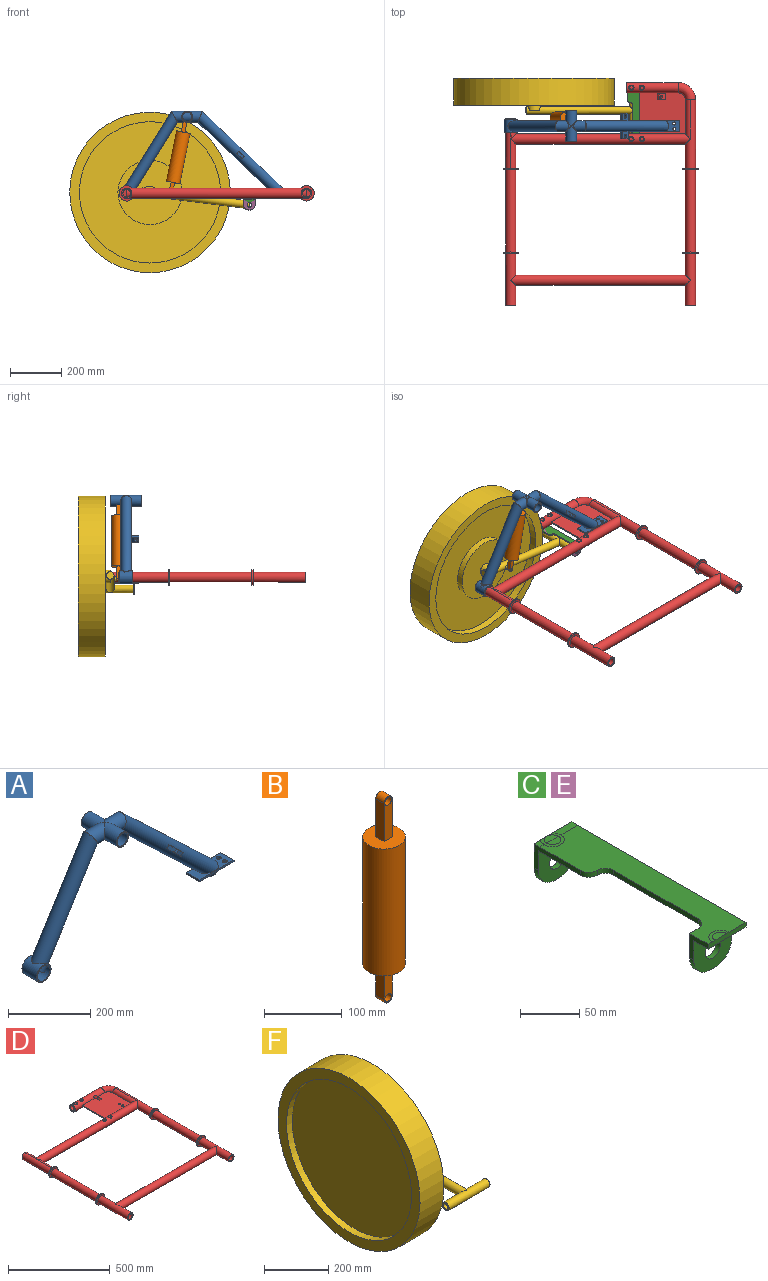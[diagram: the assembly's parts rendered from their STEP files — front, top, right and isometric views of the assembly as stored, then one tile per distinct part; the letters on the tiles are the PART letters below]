
ASSEMBLY  parts=6 mates=3
PART A: 62 faces, bbox 682.4x120x344.5 mm
  f0: cylinder r=18mm len=48.8mm, axis (0,-1,0), area 4910.4mm2, adj f2,f32
  f1: cylinder r=21.2mm len=60mm, axis (0,-1,0), area 6194.5mm2, adj f2,f13,f26
  f2: plane 42.4x42.4mm, normal (0,1,0), area 394.1mm2, adj f0,f1
  f3: cylinder r=21.2mm len=42.4mm, axis (0.73,0,-0.69), area 1202.5mm2, adj f5,f6
  f4: cylinder r=19mm len=38mm, axis (0.73,0,-0.69), area 990.8mm2, adj f5,f6
  f5: plane 42.4x17.88mm, normal (0.73,0,-0.69), area 154.2mm2, adj f3,f4,f6
  f6: plane 120x45mm, normal (0,0,-1), area 4949.8mm2, adj f3,f4,f5,f7,f8,f9,f10,f53
  f7: plane 120x5mm, normal (0,1,0), area 600mm2, adj f6,f8,f10,f11
  f8: plane 45x5mm, normal (1,0,0), area 225mm2, adj f6,f7,f9,f11
  f9: plane 120x5mm, normal (0,-1,0), area 600mm2, adj f6,f8,f10,f11
  f10: plane 45x5mm, normal (-1,0,0), area 225mm2, adj f6,f7,f9,f11
  f11: plane 120x45mm, normal (0,0,1), area 4902.5mm2, adj f7,f8,f9,f10,f12,f14,f15,f53
  f12: cylinder r=21.2mm len=349.84mm, axis (0.73,0,-0.69), area 55328.1mm2, adj f11,f13,f14,f38,f39,f40,f41,f42
  f13: cylinder r=21.2mm len=58.46mm, axis (1,0,0), area 4847.4mm2, adj f1,f12,f20
  f14: plane 37.02x7.88mm, normal (0.73,0,-0.69), area 91.1mm2, adj f11,f12,f15
  f15: cylinder r=19mm len=346.17mm, axis (0.73,0,-0.69), area 49651.3mm2, adj f11,f14,f16,f33,f34,f35,f36
  f16: cylinder r=19mm len=48.17mm, axis (1,0,0), area 4114.2mm2, adj f15,f17
  f17: cylinder r=21.2mm len=38mm, axis (0,-1,0), area 1311.6mm2, adj f16
  f18: cylinder r=18mm len=48.8mm, axis (0,-1,0), area 4909mm2, adj f19,f31
  f19: plane 42.4x42.4mm, normal (0,-1,0), area 394.1mm2, adj f18,f20
  f20: cylinder r=21.2mm len=60mm, axis (0,-1,0), area 6194.5mm2, adj f13,f19,f26
  f21: cylinder r=21.5mm len=38mm, axis (0,1,0), area 1304.9mm2, adj f24
  f22: cylinder r=21.2mm len=47.36mm, axis (0.53,0,0.85), area 1892mm2, adj f23,f30
  f23: plane 42.4x36.01mm, normal (-0.53,0,-0.85), area 277.8mm2, adj f22,f24
  f24: cylinder r=19mm len=43.62mm, axis (0.53,0,0.85), area 1946.5mm2, adj f21,f23
  f25: cylinder r=21.2mm len=319.4mm, axis (0.53,0,0.85), area 44162.7mm2, adj f26,f29
  f26: cylinder r=21.2mm len=61.78mm, axis (1,0,0), area 4849.1mm2, adj f1,f20,f25
  f27: plane 50x50mm, normal (0,1,0), area 511.3mm2, adj f29,f30
  f28: plane 50x50mm, normal (0,-1,0), area 511.3mm2, adj f29,f30
  f29: cylinder r=25mm len=50mm, axis (0,1,0), area 6256.8mm2, adj f25,f27,f28
  f30: cylinder r=21.5mm len=50mm, axis (0,1,0), area 5000.3mm2, adj f22,f27,f28
  f31: cylinder r=21.2mm len=36mm, axis (1,0,0), area 1152.3mm2, adj f18
  f32: cylinder r=21.2mm len=36mm, axis (1,0,0), area 1151.2mm2, adj f0
  f33: plane 38x7.26mm, normal (-0.73,0,0.69), area 375.6mm2, adj f15,f34,f36
  f34: plane 36.66x21.77mm, normal (0.69,0,0.73), area 1099.8mm2, adj f15,f33,f35
  f35: plane 38x7.26mm, normal (0.73,0,-0.69), area 375.6mm2, adj f15,f34,f36
  f36: plane 36.66x21.77mm, normal (-0.69,0,-0.73), area 1099.8mm2, adj f15,f33,f35
  f37: plane 21.39x21.02mm, normal (0,1,0), area 200mm2, adj f39,f41,f47,f48
  f38: plane 24.4x7.26mm, normal (-0.73,0,0.69), area 240mm2, adj f12,f39,f41,f48
  f39: plane 29.4x21.77mm, normal (0.69,0,0.73), area 717.3mm2, adj f12,f37,f38,f40,f47,f48,f52
  f40: plane 24.4x7.26mm, normal (0.73,0,-0.69), area 240mm2, adj f12,f39,f41,f47
  f41: plane 29.4x21.77mm, normal (-0.69,0,-0.73), area 717.3mm2, adj f12,f37,f38,f40,f47,f48,f52
  f42: plane 29.4x21.77mm, normal (-0.69,0,-0.73), area 717.3mm2, adj f12,f43,f45,f46,f49,f50,f51
  f43: plane 24.4x7.26mm, normal (0.73,0,-0.69), area 240mm2, adj f12,f42,f44,f49
  f44: plane 29.4x21.77mm, normal (0.69,0,0.73), area 717.3mm2, adj f12,f43,f45,f46,f49,f50,f51
  f45: plane 24.4x7.26mm, normal (-0.73,0,0.69), area 240mm2, adj f12,f42,f44,f50
  f46: plane 21.39x21.02mm, normal (0,-1,0), area 200mm2, adj f42,f44,f49,f50
  f47: cylinder r=5mm len=10.7mm, axis (0.69,0,0.73), area 78.5mm2, adj f37,f39,f40,f41
  f48: cylinder r=5mm len=10.7mm, axis (-0.69,0,-0.73), area 78.5mm2, adj f37,f38,f39,f41
  f49: cylinder r=5mm len=10.7mm, axis (-0.69,0,-0.73), area 78.5mm2, adj f42,f43,f44,f46
  f50: cylinder r=5mm len=10.7mm, axis (0.69,0,0.73), area 78.5mm2, adj f42,f44,f45,f46
  f51: cylinder r=7mm len=17.04mm, axis (0.69,0,0.73), area 439.8mm2, adj f42,f44
  f52: cylinder r=7mm len=17.04mm, axis (0.69,0,0.73), area 439.8mm2, adj f39,f41
  f53: cylinder r=6mm len=12mm, axis (0,0,1), area 188.5mm2, adj f6,f11
  f54: cylinder r=6mm len=12mm, axis (0,0,1), area 188.5mm2, adj f6,f11
  f55: cylinder r=18mm len=38mm, axis (0,-1,0), area 3028mm2, adj f56,f57
  f56: cylinder r=19mm len=36mm, axis (1,0,0), area 1218.3mm2, adj f55
  f57: cylinder r=19mm len=36mm, axis (1,0,0), area 1218.9mm2, adj f55
  f58: cylinder r=25mm len=38mm, axis (0,1,0), area 1242.2mm2, adj f59
  f59: cylinder r=19mm len=313.49mm, axis (0.53,0,0.85), area 39430.5mm2, adj f58,f60
  f60: cylinder r=19mm len=51.16mm, axis (1,0,0), area 4066.1mm2, adj f59,f61
  f61: cylinder r=21.2mm len=38mm, axis (0,-1,0), area 1313.4mm2, adj f60
PART B: 15 faces, bbox 55x55x325 mm
  f0: cylinder r=7.5mm len=15mm, axis (0,1,0), area 353.4mm2, adj f1,f2,f4,f5
  f1: plane 60x15mm, normal (-1,0,0), area 900mm2, adj f0,f4,f5,f7
  f2: plane 60x15mm, normal (1,0,0), area 900mm2, adj f0,f4,f5,f7
  f3: cylinder r=6mm len=15mm, axis (0,1,0), area 565.5mm2, adj f4,f5
  f4: plane 67.5x15mm, normal (0,-1,0), area 875.3mm2, adj f0,f1,f2,f3,f7
  f5: plane 67.5x15mm, normal (0,1,0), area 875.3mm2, adj f0,f1,f2,f3,f7
  f6: cylinder r=27.5mm len=200mm, axis (0,0,-1), area 34557.5mm2, adj f7,f8
  f7: plane 55x55mm, normal (0,0,1), area 2150.8mm2, adj f1,f2,f4,f5,f6
  f8: plane 55x55mm, normal (0,0,-1), area 2150.8mm2, adj f6,f11,f12,f13,f14
  f9: cylinder r=7.5mm len=15mm, axis (0,1,0), area 353.4mm2, adj f11,f12,f13,f14
  f10: cylinder r=6mm len=15mm, axis (0,1,0), area 565.5mm2, adj f11,f12
  f11: plane 57.5x15mm, normal (0,-1,0), area 725.3mm2, adj f8,f9,f10,f13,f14
  f12: plane 57.5x15mm, normal (0,1,0), area 725.3mm2, adj f8,f9,f10,f13,f14
  f13: plane 50x15mm, normal (1,0,0), area 750mm2, adj f8,f9,f11,f12
  f14: plane 50x15mm, normal (-1,0,0), area 750mm2, adj f8,f9,f11,f12
PART C: 30 faces, bbox 45x207x45 mm
  f0: plane 22.86x7mm, normal (0,0,1), area 146.2mm2, adj f2,f3,f6,f17
  f1: plane 7.86x7mm, normal (0,0,1), area 41.2mm2, adj f2,f5,f6,f17
  f2: plane 20x17mm, normal (0,0,1), area 130.7mm2, adj f0,f1,f6,f8,f17,f21
  f3: plane 207x25mm, normal (1,0,0), area 1235mm2, adj f0,f4,f6,f10,f12,f13,f15,f17
  f4: plane 45x40mm, normal (0,-1,0), area 1373.8mm2, adj f3,f5,f7,f9,f10,f11,f12
  f5: plane 55x25mm, normal (-1,0,0), area 375mm2, adj f1,f4,f6,f9,f12,f17,f22
  f6: plane 45x45mm, normal (0,1,0), area 1598.8mm2, adj f0,f1,f2,f3,f5,f7,f9,f10
  f7: plane 5x5mm, normal (0,0,-1), area 25mm2, adj f4,f6,f9,f10
  f8: plane 14x7mm, normal (0,0,1), area 77mm2, adj f2,f21
  f9: cylinder r=20mm len=20mm, axis (0,-1,0), area 157.1mm2, adj f4,f5,f6,f7
  f10: cylinder r=20mm len=20mm, axis (0,1,0), area 157.1mm2, adj f3,f4,f6,f7
  f11: cylinder r=9mm len=18mm, axis (0,1,0), area 282.7mm2, adj f4,f6
  f12: plane 180x45mm, normal (0,0,-1), area 5721.5mm2, adj f3,f4,f5,f15,f22,f23,f24,f25
  f13: plane 45x40mm, normal (0,-1,0), area 1373.8mm2, adj f3,f14,f16,f18,f19,f20,f26
  f14: plane 25x22mm, normal (-1,0,0), area 210mm2, adj f13,f15,f17,f18,f26,f29
  f15: plane 45x45mm, normal (0,1,0), area 1423.8mm2, adj f3,f12,f14,f16,f17,f18,f19,f20
  f16: plane 5x5mm, normal (0,0,-1), area 25mm2, adj f13,f15,f18,f19
  f17: plane 200x45mm, normal (0,0,1), area 6307.3mm2, adj f0,f1,f2,f3,f5,f14,f15,f22
  f18: cylinder r=20mm len=20mm, axis (0,-1,0), area 157.1mm2, adj f13,f14,f15,f16
  f19: cylinder r=20mm len=20mm, axis (0,1,0), area 157.1mm2, adj f3,f13,f15,f16
  f20: cylinder r=9mm len=18mm, axis (0,1,0), area 282.7mm2, adj f13,f15
  f21: plane 14x7mm, normal (0,0,1), area 77mm2, adj f2,f8
  f22: cylinder r=10mm len=10mm, axis (0,0,1), area 78.5mm2, adj f5,f12,f17,f23
  f23: cylinder r=10mm len=10mm, axis (0,0,1), area 78.5mm2, adj f12,f17,f22,f24
  f24: plane 100x5mm, normal (-1,0,0), area 500mm2, adj f12,f17,f23,f25
  f25: cylinder r=10mm len=10mm, axis (0,0,1), area 78.5mm2, adj f12,f15,f17,f24
  f26: plane 45x17mm, normal (0,0,-1), area 765mm2, adj f3,f13,f14,f29
  f27: plane 20x10mm, normal (0,0,1), area 80.1mm2, adj f17,f28,f29
  f28: plane 14x7mm, normal (0,0,1), area 77mm2, adj f27,f29
  f29: plane 45x5mm, normal (0,-1,0), area 225mm2, adj f3,f14,f17,f26,f27,f28
PART D: 178 faces, bbox 760x875.6x60 mm
  f0: plane 20x10mm, normal (0,0,-1), area 80.1mm2, adj f64,f66,f67
  f1: plane 14.28x3mm, normal (0,0,-1), area 29.5mm2, adj f16,f17
  f2: cylinder r=20mm len=14mm, axis (-1,0,0), area 78.2mm2, adj f9,f19
  f3: cylinder r=20mm len=14mm, axis (-1,0,0), area 78.2mm2, adj f62,f63
  f4: cylinder r=15mm len=30mm, axis (1,0,0), area 450mm2, adj f6,f132
  f5: cylinder r=20mm len=30mm, axis (1,0,0), area 385.9mm2, adj f6,f120
  f6: plane 30x20mm, normal (-1,0,0), area 184.2mm2, adj f4,f5,f120
  f7: cylinder r=10mm len=30mm, axis (0,0,-1), area 1653.8mm2, adj f118
  f8: cylinder r=20mm len=14mm, axis (-1,0,0), area 156.4mm2, adj f10,f11
  f9: cylinder r=20mm len=14mm, axis (-1,0,0), area 78.2mm2, adj f2,f18
  f10: cylinder r=7mm len=14mm, axis (0,0,-1), area 13.8mm2, adj f8,f14
  f11: cylinder r=7mm len=14mm, axis (0,0,-1), area 13.8mm2, adj f8,f14
  f12: cylinder r=10mm len=20mm, axis (0,0,-1), area 41.3mm2, adj f14,f117
  f13: cylinder r=10mm len=20mm, axis (0,0,-1), area 41.3mm2, adj f14,f117
  f14: plane 20x20mm, normal (0,0,1), area 160.2mm2, adj f10,f11,f12,f13
  f15: cylinder r=10mm len=20mm, axis (0,0,-1), area 41.3mm2, adj f16,f117
  f16: plane 20x17mm, normal (0,0,-1), area 130.7mm2, adj f1,f15,f17,f18,f19
  f17: cylinder r=10mm len=20mm, axis (0,0,-1), area 41.3mm2, adj f1,f16,f117
  f18: cylinder r=7mm len=14mm, axis (0,0,-1), area 13.8mm2, adj f9,f16
  f19: cylinder r=7mm len=14mm, axis (0,0,-1), area 13.8mm2, adj f2,f16
  f20: cylinder r=20mm len=14mm, axis (-1,0,0), area 156.4mm2, adj f24,f25
  f21: cylinder r=20mm len=14mm, axis (-1,0,0), area 156.4mm2, adj f30,f31
  f22: cylinder r=10mm len=20mm, axis (0,0,-1), area 41.3mm2, adj f26,f116
  f23: cylinder r=10mm len=20mm, axis (0,0,-1), area 41.3mm2, adj f26,f116
  f24: cylinder r=7mm len=14mm, axis (0,0,-1), area 13.8mm2, adj f20,f26
  f25: cylinder r=7mm len=14mm, axis (0,0,-1), area 13.8mm2, adj f20,f26
  f26: plane 20x20mm, normal (0,0,1), area 160.2mm2, adj f22,f23,f24,f25
  f27: cylinder r=10mm len=20mm, axis (0,0,-1), area 41.3mm2, adj f28,f116
  f28: plane 20x20mm, normal (0,0,-1), area 160.2mm2, adj f27,f29,f30,f31
  f29: cylinder r=10mm len=20mm, axis (0,0,-1), area 41.3mm2, adj f28,f116
  f30: cylinder r=7mm len=14mm, axis (0,0,-1), area 13.8mm2, adj f21,f28
  f31: cylinder r=7mm len=14mm, axis (0,0,-1), area 13.8mm2, adj f21,f28
  f32: cylinder r=20mm len=14mm, axis (-1,0,0), area 156.4mm2, adj f37,f38
  f33: cylinder r=20mm len=14mm, axis (-1,0,0), area 156.4mm2, adj f42,f43
  f34: cylinder r=10mm len=20mm, axis (0,0,-1), area 41.3mm2, adj f36,f117
  f35: cylinder r=10mm len=20mm, axis (0,0,-1), area 41.3mm2, adj f36,f117
  f36: plane 20x20mm, normal (0,0,1), area 160.2mm2, adj f34,f35,f37,f38
  f37: cylinder r=7mm len=14mm, axis (0,0,-1), area 13.8mm2, adj f32,f36
  f38: cylinder r=7mm len=14mm, axis (0,0,-1), area 13.8mm2, adj f32,f36
  f39: cylinder r=10mm len=20mm, axis (0,0,-1), area 41.3mm2, adj f40,f117
  f40: plane 20x20mm, normal (0,0,-1), area 160.2mm2, adj f39,f41,f42,f43
  f41: cylinder r=10mm len=20mm, axis (0,0,-1), area 41.3mm2, adj f40,f117
  f42: cylinder r=7mm len=14mm, axis (0,0,-1), area 13.8mm2, adj f33,f40
  f43: cylinder r=7mm len=14mm, axis (0,0,-1), area 13.8mm2, adj f33,f40
  f44: plane 160.31x5mm, normal (-1,0,0), area 800.5mm2, adj f45,f46,f116,f117
  f45: plane 180.16x160.31mm, normal (0,0,1), area 28184.4mm2, adj f44,f107,f108,f116,f117,f133,f134,f140
  f46: plane 180.16x160.31mm, normal (0,0,-1), area 28434.8mm2, adj f44,f107,f109,f116,f117,f133,f134,f135
  f47: cylinder r=10mm len=30mm, axis (0,0,-1), area 1496.7mm2, adj f48,f49,f50,f51,f118
  f48: plane 15x5mm, normal (-1,0,0), area 74.7mm2, adj f47,f49,f50,f118
  f49: plane 200x180.16mm, normal (0,0,1), area 4992.2mm2, adj f47,f48,f51,f52,f105,f106,f111,f112
  f50: plane 200x180.16mm, normal (0,0,-1), area 4992.2mm2, adj f47,f48,f51,f52,f105,f111,f113,f115
  f51: plane 132.5x5mm, normal (0,1,0), area 662.5mm2, adj f47,f49,f50,f52
  f52: cylinder r=47.5mm len=47.5mm, axis (0,0,-1), area 373.1mm2, adj f49,f50,f51,f105
  f53: plane 15x5mm, normal (0,-1,0), area 74.7mm2, adj f54,f55,f100,f105
  f54: plane 14.79x14.79mm, normal (0,0,1), area 218.7mm2, adj f53,f100,f104,f105
  f55: plane 14.79x14.79mm, normal (0,0,-1), area 218.7mm2, adj f53,f100,f105,f114
  f56: cylinder r=20mm len=14mm, axis (-1,0,0), area 156.4mm2, adj f57,f58
  f57: cylinder r=7mm len=14mm, axis (0,0,-1), area 13.8mm2, adj f56,f61
  f58: cylinder r=7mm len=14mm, axis (0,0,-1), area 13.8mm2, adj f56,f61
  f59: cylinder r=10mm len=20mm, axis (0,0,-1), area 41.3mm2, adj f61,f116
  f60: cylinder r=10mm len=20mm, axis (0,0,-1), area 41.3mm2, adj f61,f116
  f61: plane 20x20mm, normal (0,0,1), area 160.2mm2, adj f57,f58,f59,f60
  f62: cylinder r=20mm len=14mm, axis (-1,0,0), area 78.2mm2, adj f3,f66
  f63: cylinder r=7mm len=14mm, axis (0,0,-1), area 13.8mm2, adj f3,f64
  f64: plane 20x10mm, normal (0,0,-1), area 80.1mm2, adj f0,f63,f65
  f65: cylinder r=10mm len=20mm, axis (0,0,-1), area 41.3mm2, adj f64,f116
  f66: cylinder r=7mm len=14mm, axis (0,0,-1), area 13.8mm2, adj f0,f62
  f67: cylinder r=10mm len=20mm, axis (0,0,-1), area 41.3mm2, adj f0,f116
  f68: cylinder r=20mm len=320mm, axis (0,1,0), area 40212.4mm2, adj f69,f78
  f69: plane 60x60mm, normal (0,1,0), area 1570.8mm2, adj f68,f70
  f70: cylinder r=30mm len=60mm, axis (0,1,0), area 942.5mm2, adj f69,f71
  f71: plane 60x60mm, normal (0,-1,0), area 1570.8mm2, adj f70,f72
  f72: cylinder r=20mm len=205mm, axis (0,1,0), area 24161.1mm2, adj f71,f73,f121
  f73: plane 40x40mm, normal (0,-1,0), area 549.8mm2, adj f72,f119
  f74: plane 30x30mm, normal (0,-1,0), area 706.9mm2, adj f119
  f75: plane 30x30mm, normal (0,1,0), area 706.9mm2, adj f113
  f76: cylinder r=30mm len=60mm, axis (0,-1,0), area 942.5mm2, adj f77,f78
  f77: plane 60x60mm, normal (0,1,0), area 1570.8mm2, adj f76,f109
  f78: plane 60x60mm, normal (0,-1,0), area 1570.8mm2, adj f68,f76
  f79: cylinder r=15mm len=30.1mm, axis (0,1,0), area 900mm2, adj f82,f85
  f80: cylinder r=20mm len=30mm, axis (-1,0,0), area 386mm2, adj f81,f98
  f81: plane 30x20mm, normal (-1,0,0), area 184.2mm2, adj f80,f82,f98
  f82: cylinder r=15mm len=30mm, axis (-1,0,0), area 450mm2, adj f79,f81
  f83: cylinder r=20mm len=30mm, axis (-1,0,0), area 386mm2, adj f84,f98
  f84: plane 30x20mm, normal (-1,0,0), area 184.2mm2, adj f83,f85,f98
  f85: cylinder r=15mm len=30mm, axis (-1,0,0), area 450mm2, adj f79,f84
  f86: plane 30x30mm, normal (0,-1,0), area 706.9mm2, adj f120
  f87: plane 40x40mm, normal (0,-1,0), area 549.8mm2, adj f88,f120
  f88: cylinder r=20mm len=205mm, axis (0,1,0), area 24161.1mm2, adj f87,f96,f121
  f89: plane 40x40mm, normal (0,1,0), area 549.8mm2, adj f98,f99
  f90: plane 60x60mm, normal (0,-1,0), area 1570.8mm2, adj f92,f94
  f91: plane 60x60mm, normal (0,1,0), area 1570.8mm2, adj f92,f99
  f92: cylinder r=30mm len=60mm, axis (0,-1,0), area 942.5mm2, adj f90,f91
  f93: plane 30x30mm, normal (0,1,0), area 706.9mm2, adj f98
  f94: cylinder r=20mm len=320mm, axis (0,1,0), area 40212.4mm2, adj f90,f95
  f95: plane 60x60mm, normal (0,1,0), area 1570.8mm2, adj f94,f97
  f96: plane 60x60mm, normal (0,-1,0), area 1570.8mm2, adj f88,f97
  f97: cylinder r=30mm len=60mm, axis (0,1,0), area 942.5mm2, adj f95,f96
  f98: cylinder r=15mm len=195mm, axis (0,1,0), area 16796.1mm2, adj f80,f81,f83,f84,f89,f93
  f99: cylinder r=20mm len=195mm, axis (0,1,0), area 22904.4mm2, adj f89,f91,f116
  f100: cylinder r=15mm len=30mm, axis (0,1,0), area 825mm2, adj f53,f54,f55,f103,f104,f114
  f101: cylinder r=20mm len=30mm, axis (-1,0,0), area 386mm2, adj f102,f113
  f102: plane 30x20mm, normal (1,0,0), area 184.2mm2, adj f101,f103,f113
  f103: cylinder r=15mm len=30mm, axis (-1,0,0), area 450mm2, adj f100,f102
  f104: cylinder r=15mm len=14.79mm, axis (-1,0,0), area 187.5mm2, adj f54,f100,f105
  f105: plane 152.5x30mm, normal (1,0,0), area 921.6mm2, adj f49,f50,f52,f53,f54,f55,f104,f106
  f106: cylinder r=20mm len=14.79mm, axis (-1,0,0), area 155.5mm2, adj f49,f105,f112
  f107: torus R=47.5mm, axis (0,0,1), area 9159.2mm2, adj f45,f46,f108,f109,f117
  f108: cylinder r=20mm len=152.5mm, axis (0,1,0), area 4058.7mm2, adj f45,f107,f109,f116
  f109: cylinder r=20mm len=267.5mm, axis (0,1,0), area 27291.9mm2, adj f46,f77,f107,f108,f116
  f110: plane 40x40mm, normal (-1,0,0), area 549.8mm2, adj f117,f118
  f111: torus R=47.5mm, axis (0,0,1), area 6775.1mm2, adj f49,f50,f112,f113,f118
  f112: cylinder r=15mm len=139.27mm, axis (0,1,0), area 2864.7mm2, adj f49,f106,f111,f113
  f113: cylinder r=15mm len=267.5mm, axis (0,1,0), area 20098.5mm2, adj f50,f75,f101,f102,f105,f111,f112,f115
  f114: cylinder r=15mm len=14.79mm, axis (-1,0,0), area 187.5mm2, adj f55,f100,f105
  f115: cylinder r=20mm len=14.79mm, axis (-1,0,0), area 155.5mm2, adj f50,f105,f113
  f116: cylinder r=20mm len=700mm, axis (-1,0,0), area 82561.9mm2, adj f22,f23,f27,f29,f44,f45,f46,f59
  f117: cylinder r=20mm len=202.5mm, axis (-1,0,0), area 23382.6mm2, adj f12,f13,f15,f17,f34,f35,f39,f41
  f118: cylinder r=15mm len=202.5mm, axis (-1,0,0), area 16979.3mm2, adj f7,f47,f48,f49,f50,f110,f111
  f119: cylinder r=15mm len=205mm, axis (0,1,0), area 17738.6mm2, adj f73,f74,f122,f123,f125,f126
  f120: cylinder r=15mm len=205mm, axis (0,1,0), area 17738.6mm2, adj f5,f6,f86,f87,f128,f129
  f121: cylinder r=20mm len=700mm, axis (1,0,0), area 84764.6mm2, adj f72,f88
  f122: cylinder r=20mm len=30mm, axis (1,0,0), area 386mm2, adj f119,f123
  f123: plane 30x20mm, normal (1,0,0), area 184.2mm2, adj f119,f122,f124
  f124: cylinder r=15mm len=30mm, axis (1,0,0), area 450mm2, adj f123,f131
  f125: cylinder r=20mm len=30mm, axis (1,0,0), area 386mm2, adj f119,f126
  f126: plane 30x20mm, normal (1,0,0), area 184.2mm2, adj f119,f125,f127
  f127: cylinder r=15mm len=30mm, axis (1,0,0), area 450mm2, adj f126,f131
  f128: cylinder r=20mm len=30mm, axis (1,0,0), area 385.9mm2, adj f120,f129
  f129: plane 30x20mm, normal (-1,0,0), area 184.2mm2, adj f120,f128,f130
  f130: cylinder r=15mm len=30mm, axis (1,0,0), area 450mm2, adj f129,f132
  f131: cylinder r=15mm len=30.1mm, axis (0,1,0), area 900mm2, adj f124,f127
  f132: cylinder r=15mm len=30.1mm, axis (0,1,0), area 900mm2, adj f4,f130
  f133: cylinder r=6mm len=12mm, axis (0,0,1), area 188.5mm2, adj f45,f46
  f134: cylinder r=6mm len=12mm, axis (0,0,1), area 188.5mm2, adj f45,f46
  f135: plane 25x1.19mm, normal (-0.69,0,-0.73), area 41mm2, adj f46,f136,f137,f138
  f136: plane 2.26x1.13mm, normal (0,1,0), area 1.3mm2, adj f46,f135,f137
  f137: plane 25x1.13mm, normal (0.73,0,-0.69), area 38.9mm2, adj f46,f135,f136,f138
  f138: plane 2.26x1.13mm, normal (0,-1,0), area 1.3mm2, adj f46,f135,f137
  f139: plane 15x7.26mm, normal (-0.73,0,0.69), area 150mm2, adj f144,f145,f146,f147
  f140: plane 28.65x21.77mm, normal (0,-1,0), area 262.4mm2, adj f45,f141,f144,f145,f146
  f141: plane 25x1.13mm, normal (0.73,0,-0.69), area 38.9mm2, adj f45,f140,f143,f145
  f142: cylinder r=6mm len=15.59mm, axis (0.69,0,0.73), area 377mm2, adj f144,f145
  f143: plane 28.65x21.77mm, normal (0,1,0), area 262.4mm2, adj f45,f141,f144,f145,f147
  f144: plane 25x18.93mm, normal (-0.69,0,-0.73), area 528.5mm2, adj f45,f139,f140,f142,f143,f146,f147
  f145: plane 25.4x25mm, normal (0.69,0,0.73), area 751.2mm2, adj f139,f140,f141,f142,f143,f146,f147
  f146: cylinder r=5mm len=10.7mm, axis (-0.69,0,-0.73), area 78.5mm2, adj f139,f140,f144,f145
  f147: cylinder r=5mm len=10.7mm, axis (0.69,0,0.73), area 78.5mm2, adj f139,f143,f144,f145
  f148: cylinder r=20mm len=30mm, axis (0,1,0), area 772mm2, adj f149
  f149: cylinder r=15mm len=673.55mm, axis (1,0,0), area 62809mm2, adj f148,f150
  f150: cylinder r=20mm len=30mm, axis (0,1,0), area 771.9mm2, adj f149
  f151: cylinder r=7mm len=30mm, axis (0,0,-1), area 1244.4mm2, adj f152,f153
  f152: cylinder r=15mm len=14mm, axis (-1,0,0), area 158.5mm2, adj f151
  f153: cylinder r=15mm len=14mm, axis (-1,0,0), area 158.5mm2, adj f151
  f154: cylinder r=7mm len=30mm, axis (0,0,-1), area 1244.4mm2, adj f155,f156
  f155: cylinder r=15mm len=14mm, axis (-1,0,0), area 158.5mm2, adj f154
  f156: cylinder r=15mm len=14mm, axis (-1,0,0), area 158.5mm2, adj f154
  f157: cylinder r=7mm len=30mm, axis (0,0,-1), area 1244.4mm2, adj f158,f159
  f158: cylinder r=15mm len=14mm, axis (-1,0,0), area 158.5mm2, adj f157
  f159: cylinder r=15mm len=14mm, axis (-1,0,0), area 158.5mm2, adj f157
  f160: plane 30x30mm, normal (0,1,0), area 706.9mm2, adj f161
  f161: cylinder r=15mm len=320mm, axis (0,1,0), area 30159.3mm2, adj f160,f162
  f162: plane 30x30mm, normal (0,-1,0), area 706.9mm2, adj f161
  f163: cylinder r=15mm len=673.55mm, axis (-1,0,0), area 60565.1mm2, adj f164,f165,f166,f167,f168,f170,f171
  f164: cylinder r=20mm len=30mm, axis (0,1,0), area 772.1mm2, adj f163
  f165: cylinder r=20mm len=30mm, axis (0,1,0), area 696.9mm2, adj f163,f167,f168,f169
  f166: cylinder r=10mm len=30mm, axis (0,0,-1), area 1653.8mm2, adj f163
  f167: plane 180.16x14.79mm, normal (0,0,1), area 2507.5mm2, adj f163,f165,f169,f170,f171
  f168: plane 180.16x14.79mm, normal (0,0,-1), area 2507.5mm2, adj f163,f165,f169,f170,f171
  f169: plane 160.16x5mm, normal (0,-1,0), area 800.3mm2, adj f165,f167,f168,f171
  f170: plane 15x5mm, normal (-1,0,0), area 74.7mm2, adj f163,f167,f168,f171
  f171: cylinder r=10mm len=30mm, axis (0,0,-1), area 1496.7mm2, adj f163,f167,f168,f169,f170
  f172: plane 30x30mm, normal (0,-1,0), area 706.9mm2, adj f173
  f173: cylinder r=15mm len=320mm, axis (0,1,0), area 30159.3mm2, adj f172,f174
  f174: plane 30x30mm, normal (0,1,0), area 706.9mm2, adj f173
  f175: cylinder r=7mm len=30mm, axis (0,0,-1), area 1244.4mm2, adj f176,f177
  f176: cylinder r=15mm len=14mm, axis (-1,0,0), area 158.5mm2, adj f175
  f177: cylinder r=15mm len=14mm, axis (-1,0,0), area 158.5mm2, adj f175
PART E: same geometry as C
PART F: 23 faces, bbox 215x717.5x625 mm
  f0: cylinder r=15mm len=420mm, axis (0,1,0), area 36441.3mm2, adj f4,f5,f9,f10,f11,f21
  f1: cylinder r=9.5mm len=180mm, axis (1,0,0), area 9946.9mm2, adj f2,f3,f6,f7,f8
  f2: plane 30x30mm, normal (-1,0,0), area 423.3mm2, adj f1,f4
  f3: plane 30x30mm, normal (1,0,0), area 423.3mm2, adj f1,f4
  f4: cylinder r=15mm len=180mm, axis (1,0,0), area 16064.6mm2, adj f0,f2,f3
  f5: plane 30x30mm, normal (0,1,0), area 706.9mm2, adj f0
  f6: cylinder r=15mm len=19mm, axis (0,1,0), area 150.2mm2, adj f1,f8
  f7: cylinder r=15mm len=19mm, axis (0,1,0), area 150.2mm2, adj f1,f8
  f8: plane 30x19mm, normal (0,-1,0), area 529.2mm2, adj f1,f6,f7
  f9: plane 40x10mm, normal (1,0,0), area 279.6mm2, adj f0,f10
  f10: cylinder r=25mm len=50mm, axis (1,0,0), area 3182.5mm2, adj f0,f9,f11,f13
  f11: plane 40x10mm, normal (1,0,0), area 279.6mm2, adj f0,f10
  f12: cylinder r=125mm len=250mm, axis (1,0,0), area 19635mm2, adj f13,f14
  f13: plane 250x250mm, normal (1,0,0), area 47123.9mm2, adj f10,f12
  f14: plane 550x550mm, normal (1,0,0), area 188495.6mm2, adj f12,f15
  f15: cylinder r=275mm len=550mm, axis (1,0,0), area 51836.3mm2, adj f14,f16
  f16: plane 625x625mm, normal (1,0,0), area 69213.2mm2, adj f15,f17
  f17: cylinder r=312.5mm len=625mm, axis (1,0,0), area 206167mm2, adj f16,f19
  f18: cylinder r=275mm len=550mm, axis (1,0,0), area 43196.9mm2, adj f19,f20
  f19: plane 625x625mm, normal (-1,0,0), area 69213.2mm2, adj f17,f18
  f20: plane 550x550mm, normal (-1,0,0), area 237582.9mm2, adj f18
  f21: cylinder r=6mm len=26.25mm, axis (-1,0,0), area 965.8mm2, adj f0,f22
  f22: plane 12x12mm, normal (1,0,0), area 113.1mm2, adj f21
PLACE A t=(-541.16,-143.45,634.64)mm
PLACE B rot(axis=(0,1,0),11.4deg) t=(-371.26,586.05,628.15)mm
PLACE C t=(-541.16,-143.45,634.64)mm fixed
PLACE D t=(-541.16,-143.45,634.64)mm fixed
PLACE E t=(-541.16,-143.45,634.64)mm
PLACE F rot(axis=(0.71,-0.71,-0.04),175deg) t=(-63.66,708.55,589.64)mm
MATE fastened D.f133 <-> A.f53  axis (0,0,1) through (96.2,567.05,637.14)mm
MATE revolute C.f11 <-> F.f1  axis (0,1,0) through (-63.66,528.55,589.64)mm
MATE revolute F.f21 <-> B.f10  axis (0,-1,0) through (-371.26,578.55,628.15)mm
